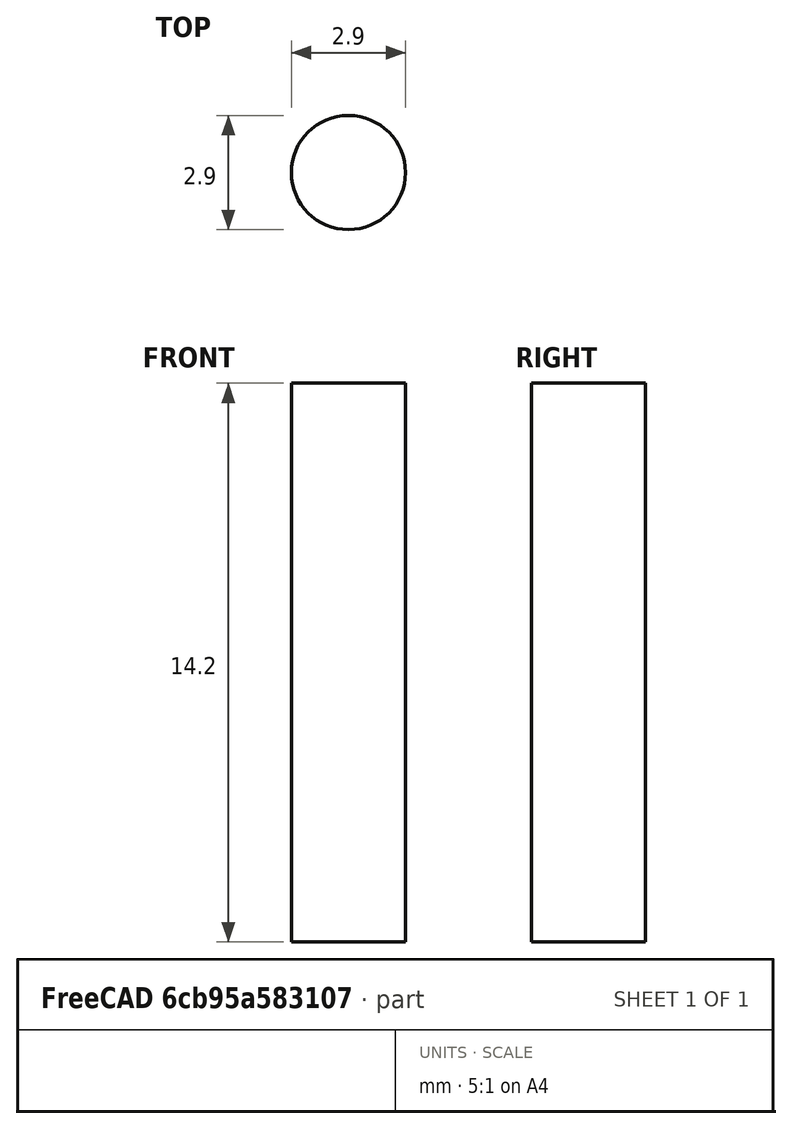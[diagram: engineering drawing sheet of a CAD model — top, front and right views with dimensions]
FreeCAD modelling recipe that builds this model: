
FCSTD DOCUMENT  (FreeCAD 1.0R39319 (Git))
Label: MAGNET-D3x14
License: All rights reserved
LicenseURL: http://en.wikipedia.org/wiki/All_rights_reserved
objects: TechDraw::DrawGeomHatch×4, TechDraw::DrawProjGroupItem×3, TechDraw::DrawViewDimension×2, TechDraw::DrawViewBalloon×2, Sketcher::SketchObject×1, PartDesign::Pad×1, TechDraw::DrawViewAnnotation×1, PartDesign::Mirrored×1, TechDraw::DrawSVGTemplate×1, PartDesign::Plane×1, PartDesign::Line×1, PartDesign::Body×1, TechDraw::DrawProjGroup×1, TechDraw::DrawPage×1
note: 12 computed .brp shape members not serialized (recipe doc carries the construction recipe); baked Part::Feature solids carry a one-line shape summary decoded from their .brp

FEATURE [Sketcher::SketchObject] Sketch001
  ArcFitTolerance = 0
  AttachmentSupport = -> [XY_Plane001]
  FullyConstrained = true
  MakeInternals = false
  MapMode = 5
  sketch-geometry (2):
    g0: ArcOfCircle CenterX=0 CenterY=0 CenterZ=0 NormalX=0 NormalY=0 NormalZ=1 AngleXU=0 Radius=1.45 StartAngle=1.5708 EndAngle=4.71239
    g1: LineSegment StartX=0 StartY=-1.45 StartZ=0 EndX=1e-16 EndY=1.45 EndZ=0
  constraints (6):
    c: Coincident(g0,g-1)
    c: PointOnObject(g0,g-2)
    c: PointOnObject(g0,g-2)
    c: Radius(g0) = 1.45
    c: Coincident(g1,g0)
    c: Coincident(g1,g0)
FEATURE [PartDesign::Pad] Pad001  label="RodN"
  AllowMultiFace = false
  Direction = (0,0,1)
  Length = 14.2
  Length2 = 100
  Profile = -> Sketch001
  ReferenceAxis = -> Sketch001 [N_Axis]
  Refine = true
  Suppressed = false
  Type = 0
FEATURE [TechDraw::DrawViewAnnotation] Annotation
  Font = osifont
  LineSpace = 80
  LockPosition = false
  MaxWidth = -1
  Rotation = 0
  Scale = 3
  ScaleType = 0
  Text = Minimum Magnet Grade: N52
  TextSize = 5
  TextStyle = 0
  X = 87.2293
  Y = 185.906
FEATURE [PartDesign::Mirrored] Mirrored
  BaseFeature = -> Pad001
  MirrorPlane = -> Sketch001 [V_Axis]
  Originals = -> [Pad001]
  Suppressed = false
  TransformMode = 0
FEATURE [TechDraw::DrawSVGTemplate] Template
  EditableTexts = Designed_by_Name=Designed by Name; Drawing_number=Drawing number; FC-Date=2025.06.23.; FC-SC=Scale; FC-SH=Sheet; FC-Title=Title; Subtitle=Subtitle; Weight=Weight
  Height = 210
  Orientation = 1
  Template = /snap/freecad/759/usr/share/Mod/TechDraw/Templates/A4_LandscapeTD.svg
  Width = 297
FEATURE [PartDesign::Plane] Plane_1
  AttachmentSupport = -> [Mirrored]
  Length = 100
  MapMode = 5
  Placement = pos=(0,0,14.2) rot=(0,0,1;0rad)
  ResizeMode = 1
  Width = 100
FEATURE [PartDesign::Line] Axis_1
  AttacherType = Attacher::AttachEngineLine
  Length = 200
  ResizeMode = 1
FEATURE [PartDesign::Body] Body001  label="MAGNET-D3x14"
  AllowCompound = false
  Group = -> [Sketch001,Pad001,Mirrored,Plane_1,Axis_1]
  Origin = -> Origin001
  Placement = pos=(0,0,0) rot=(0,0,1;3.14159rad)
  Tip = -> Mirrored
FEATURE [TechDraw::DrawProjGroupItem] ProjItem  label="Front"
  CoarseView = false
  Direction = (0,-1,0)
  Focus = 100
  HardHidden = false
  IsoCount = 0
  IsoHidden = false
  IsoVisible = false
  LockPosition = true
  Perspective = false
  Rotation = 0
  RotationVector = (1,0,0)
  ScaleType = 2
  ScrubCount = 0
  SeamHidden = false
  SeamVisible = false
  SmoothHidden = false
  SmoothVisible = true
  Source = -> [Body001]
  Type = 0
  X = 0
  XDirection = (1,0,0)
  Y = 0
FEATURE [TechDraw::DrawProjGroupItem] ProjItem012  label="Left001"
  CoarseView = false
  Direction = (-1,-1e-16,0)
  Focus = 100
  HardHidden = false
  IsoCount = 0
  IsoHidden = false
  IsoVisible = false
  LockPosition = false
  Perspective = false
  Rotation = 0
  RotationVector = (1,0,0)
  ScaleType = 2
  ScrubCount = 0
  SeamHidden = false
  SeamVisible = false
  SmoothHidden = false
  SmoothVisible = true
  Source = -> [Body001]
  Type = 1
  X = 38.7
  XDirection = (1e-16,-1,0)
  Y = 0
FEATURE [TechDraw::DrawProjGroupItem] ProjItem013  label="FrontBottomLeft001"
  CoarseView = false
  Direction = (-0.57735,-0.57735,-0.57735)
  Focus = 100
  HardHidden = false
  IsoCount = 0
  IsoHidden = false
  IsoVisible = false
  LockPosition = false
  Perspective = false
  Rotation = 0
  RotationVector = (1,0,0)
  ScaleType = 2
  ScrubCount = 0
  SeamHidden = false
  SeamVisible = false
  SmoothHidden = false
  SmoothVisible = true
  Source = -> [Body001]
  Type = 8
  X = 38.7
  XDirection = (0.707107,-0.707107,0)
  Y = 71.2029
FEATURE [TechDraw::DrawProjGroup] ProjGroup
  Anchor = -> ProjItem
  AutoDistribute = true
  LockPosition = false
  ProjectionType = 0
  Rotation = 0
  Scale = 3
  ScaleType = 0
  Source = -> [Body001]
  Views = -> [ProjItem,ProjItem012,ProjItem013]
  X = 50
  Y = 75
  spacingX = 30
  spacingY = 30
FEATURE [TechDraw::DrawViewDimension] Dimension003
  AngleOverride = false
  Arbitrary = false
  ArbitraryTolerances = false
  EqualTolerance = true
  ExtensionAngle = 0
  FormatSpec = %.2w
  FormatSpecOverTolerance = %+.2w
  FormatSpecUnderTolerance = %+.2w
  Inverted = false
  LineAngle = 0
  LockPosition = false
  MeasureType = 1
  OverTolerance = 0
  References2D = -> [ProjItem]
  Rotation = 0
  Scale = 3
  ScaleType = 0
  TheoreticalExact = false
  Type = 2
  UnderTolerance = 0
  X = -18.0773
  Y = 1.76609
FEATURE [TechDraw::DrawViewDimension] Dimension004
  AngleOverride = false
  Arbitrary = false
  ArbitraryTolerances = false
  EqualTolerance = true
  ExtensionAngle = 0
  FormatSpec = ⌀%.2w
  FormatSpecOverTolerance = %+.2w
  FormatSpecUnderTolerance = %+.2w
  Inverted = false
  LineAngle = 0
  LockPosition = false
  MeasureType = 1
  OverTolerance = 0
  References2D = -> [ProjItem012]
  Rotation = 0
  Scale = 3
  ScaleType = 0
  TheoreticalExact = false
  Type = 1
  UnderTolerance = 0
  X = -14.3762
  Y = 33.435
FEATURE [TechDraw::DrawViewBalloon] Balloon002
  BubbleShape = 6
  EndType = 1
  EndTypeScale = 1
  KinkLength = 5
  LockPosition = false
  OriginX = -2.03
  OriginY = 1.13805
  Rotation = 0
  Scale = 3
  ScaleType = 0
  ShapeScale = 1
  SourceView = -> ProjItem013
  Text = North
  TextWrapLen = -1
  X = -10.3087
  Y = 3.48898
FEATURE [TechDraw::DrawViewBalloon] Balloon003
  BubbleShape = 6
  EndType = 1
  EndTypeScale = 1
  KinkLength = 5
  LockPosition = false
  OriginX = 2.24
  OriginY = -1.72306
  Rotation = 0
  Scale = 3
  ScaleType = 0
  ShapeScale = 1
  SourceView = -> ProjItem013
  Text = South
  TextWrapLen = -1
  X = 12.1747
  Y = -5.18693
FEATURE [TechDraw::DrawPage] Page  label="MAGNET-D3x14_Drawing"
  KeepUpdated = true
  NextBalloonIndex = 5
  ProjectionType = 0
  Scale = 3
  Template = -> Template
  Views = -> [Annotation,ProjGroup,Dimension003,Dimension004,Balloon002,Balloon003]
FEATURE [TechDraw::DrawGeomHatch] GeomHatch
  FilePattern = /snap/freecad/1248/usr/share/Mod/TechDraw/PAT/FCPAT.pat
  NamePattern = Diamond
  PatternOffset = (0,0,0)
  PatternRotation = 0
  ScalePattern = 1
  Source = -> ProjItem013 [Face1]
FEATURE [TechDraw::DrawGeomHatch] GeomHatch001
  FilePattern = /snap/freecad/1248/usr/share/Mod/TechDraw/PAT/FCPAT.pat
  NamePattern = Diamond
  PatternOffset = (0,0,0)
  PatternRotation = 0
  ScalePattern = 1
  Source = -> ProjItem013 [Face4]
FEATURE [TechDraw::DrawGeomHatch] GeomHatch002
  FilePattern = /snap/freecad/1248/usr/share/Mod/TechDraw/PAT/FCPAT.pat
  NamePattern = Diamond
  PatternOffset = (0,0,0)
  PatternRotation = 0
  ScalePattern = 1
  Source = -> ProjItem013 [Face3]
FEATURE [TechDraw::DrawGeomHatch] GeomHatch003
  FilePattern = /snap/freecad/1248/usr/share/Mod/TechDraw/PAT/FCPAT.pat
  NamePattern = Diamond
  PatternOffset = (0,0,0)
  PatternRotation = 0
  ScalePattern = 1
  Source = -> ProjItem013 [Face2]
